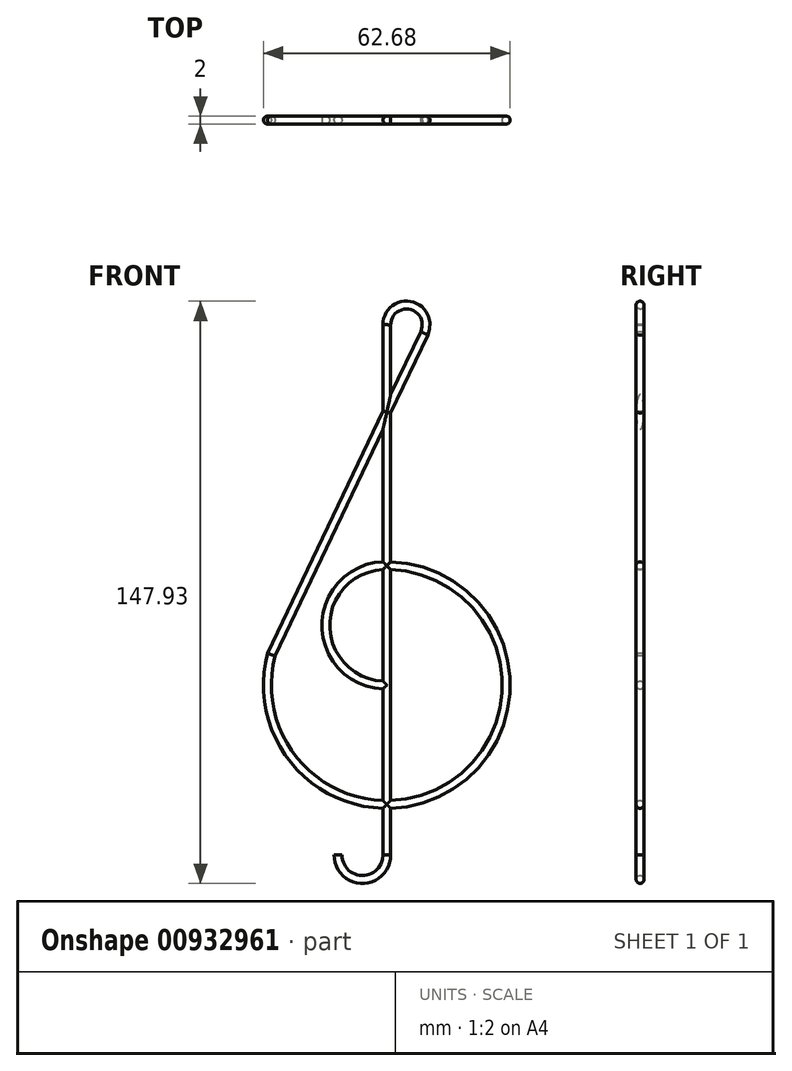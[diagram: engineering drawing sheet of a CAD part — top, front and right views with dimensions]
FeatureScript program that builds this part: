
annotation { "Feature Type Name" : "Feature", "Feature Type Description" : "" }
export const myFeature = defineFeature(function(context is Context, id is Id, definition is map)
    precondition{}
    {
        {
            var Q0;
            Q0=qCreatedBy(makeId("Front.planeOp"),FACE);
            var sketch = newSketch(context, id + "F0", { "sketchPlane" : qUnion([Q0])});
            skArc(sketch, "E0", {"start": v(-29.35, 7.7) * mm, "mid": v(18.53, -24.02) * mm, "end": v(0, 30.34) * mm});
            skArc(sketch, "E1", {"start": v(0, 30.34) * mm, "mid": v(-15.51, 15.17) * mm, "end": v(0, 0) * mm});
            skLineSegment(sketch, "E2", {"start": v(-29.35, 7.7) * mm, "end": v(9.52, 89.39) * mm});
            skLineSegment(sketch, "E3", {"start": v(0, 91.54) * mm, "end": v(0, 30.34) * mm});
            skArc(sketch, "E4", {"start": v(-12.4, -43.2) * mm, "mid": v(-6.2, -49.4) * mm, "end": v(0, -43.2) * mm});
            skLineSegment(sketch, "E5.trimOffspring", {"start": v(0, 0) * mm, "end": v(0, -43.2) * mm});
            skLineSegment(sketch, "E6", {"start": v(0, 30.34) * mm, "end": v(0, 0) * mm});
            skArc(sketch, "E7", {"start": v(9.52, 89.39) * mm, "mid": v(6.1, 96.41) * mm, "end": v(0, 91.54) * mm});
            skSolve(sketch);
        }
        {
            var Q0;
            Q0=qCreatedBy(makeId("Right.planeOp"),FACE);
            var sketch = newSketch(context, id + "F1", { "sketchPlane" : qUnion([Q0])});
            skCircle(sketch, "E8", {"center": v(0, 0) * mm, "radius": 1 * mm});
            skSolve(sketch);
        }
        {
            var Q0;
            Q0 = qSketchRegion(id + "F1", true);
            var Q1;
            Q1=sQuery(id+"F0.wireOp",EDGE,"E1");
            var Q2;
            Q2=sQuery(id+"F0.wireOp",EDGE,"E0");
            var Q3;
            Q3=sQuery(id+"F0.wireOp",EDGE,"E2");
            var Q4;
            Q4=sQuery(id+"F0.wireOp",EDGE,"save4uHq-6Z80-mI7T-tfgD-DMVLavORQVnd");
            var Q5;
            Q5=sQuery(id+"F0.wireOp",EDGE,"E7");
            sweep(context, id + "F2", {"profiles" : qUnion([Q0]), "path" : qUnion([Q1, Q2, Q3, Q4, Q5])});
        }
        {
            var Q0;
            Q0=makeQuery(id+"F2.opSweep","CAP_FACE",FACE,{"disambiguationData":[OSD([sQuery(id+"F0.wireOp",VERTEX,"E7.end"),sQuery(id+"F1.wireOp",EDGE,"E8")])],"isStart":false});
            var sketch = newSketch(context, id + "F3", { "sketchPlane" : qUnion([Q0])});
            skSolve(sketch);
        }
        {
            var Q0;
            Q0=makeQuery(id+"F3.imprint","IMPRINT",FACE,{"disambiguationData":[TD([[makeQuery(id+"F3.imprint","IMPRINT",EDGE,{"derivedFrom":makeQuery(id+"F2.opSweep","CAP_EDGE",EDGE,{"disambiguationData":[OSD([sQuery(id+"F0.wireOp",VERTEX,"E7.end"),sQuery(id+"F1.wireOp",EDGE,"E8")])],"isStart":false})}),1.0]])]});
            var Q1;
            Q1=sQuery(id+"F0.wireOp",EDGE,"E3");
            var Q2;
            Q2=sQuery(id+"F0.wireOp",EDGE,"E6");
            var Q3;
            Q3=sQuery(id+"F0.wireOp",EDGE,"E5.trimOffspring");
            var Q4;
            Q4=sQuery(id+"F0.wireOp",EDGE,"E4");
            sweep(context, id + "F4", {"operationType" : NewBodyOperationType.ADD, "profiles" : qUnion([Q0]), "path" : qUnion([Q1, Q2, Q3, Q4])});
        }
    });
